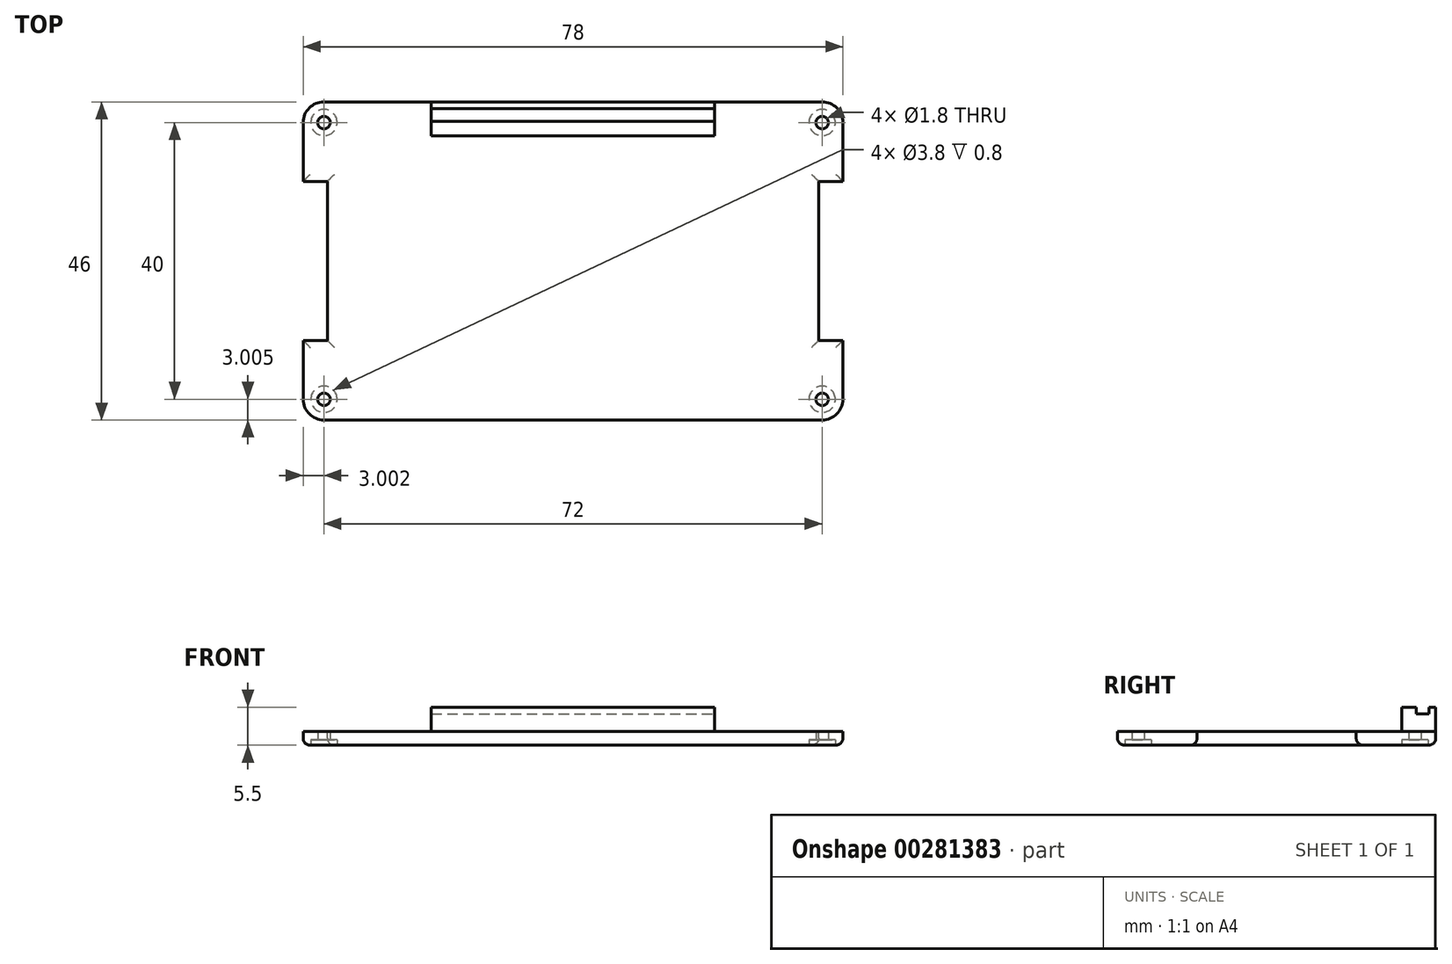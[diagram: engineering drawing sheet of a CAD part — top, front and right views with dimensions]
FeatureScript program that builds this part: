
annotation { "Feature Type Name" : "Feature", "Feature Type Description" : "" }
export const myFeature = defineFeature(function(context is Context, id is Id, definition is map)
    precondition{}
    {
        {
            var Q0;
            Q0=qCreatedBy(makeId("Top.planeOp"),FACE);
            var sketch = newSketch(context, id + "F0", { "sketchPlane" : qUnion([Q0])});
            skLineSegment(sketch, "E0.bottom", {"start": v(-44.88, 28.76) * mm, "end": v(33.12, 28.76) * mm});
            skLineSegment(sketch, "E0.top", {"start": v(-44.88, -17.24) * mm, "end": v(33.12, -17.24) * mm});
            skLineSegment(sketch, "E0.left", {"start": v(-44.88, 28.76) * mm, "end": v(-44.88, -17.24) * mm});
            skLineSegment(sketch, "E0.right", {"start": v(33.12, 28.76) * mm, "end": v(33.12, -17.24) * mm});
            skLineSegment(sketch, "E1.bottom", {"start": v(-44.88, 17.26) * mm, "end": v(-41.38, 17.26) * mm});
            skLineSegment(sketch, "E1.top", {"start": v(-44.88, -5.74) * mm, "end": v(-41.38, -5.74) * mm});
            skLineSegment(sketch, "E1.left", {"start": v(-44.88, 17.26) * mm, "end": v(-44.88, -5.74) * mm});
            skLineSegment(sketch, "E1.right", {"start": v(-41.38, 17.26) * mm, "end": v(-41.38, -5.74) * mm});
            skLineSegment(sketch, "E2.bottom", {"start": v(33.12, 17.26) * mm, "end": v(29.62, 17.26) * mm});
            skLineSegment(sketch, "E2.top", {"start": v(33.12, -5.74) * mm, "end": v(29.62, -5.74) * mm});
            skLineSegment(sketch, "E2.left", {"start": v(33.12, 17.26) * mm, "end": v(33.12, -5.74) * mm});
            skLineSegment(sketch, "E2.right", {"start": v(29.62, 17.26) * mm, "end": v(29.62, -5.74) * mm});
            skSolve(sketch);
        }
        {
            var Q0;
            {var subQ7=sQuery(id+"F0.wireOp",EDGE,"E0.bottom");Q0=makeQuery(id+"F0.imprint","IMPRINT",FACE,{"disambiguationData":[TD([[makeQuery(id+"F0.imprint","IMPRINT",EDGE,{"derivedFrom":subQ7}),-1.0]])]});}
            extrude(context, id + "F1", {"entities" : qUnion([Q0]), "depth" : 2 * mm});
        }
        {
            var Q0;
            Q0=makeQuery(id+"F1.opExtrude","SWEPT_EDGE",EDGE,{"disambiguationData":[OSD([sQuery(id+"F0.wireOp",EDGE,"E0.bottom"),sQuery(id+"F0.wireOp",EDGE,"E0.left")])]});
            var Q1;
            Q1=makeQuery(id+"F1.opExtrude","SWEPT_EDGE",EDGE,{"disambiguationData":[OSD([sQuery(id+"F0.wireOp",EDGE,"E0.bottom"),sQuery(id+"F0.wireOp",EDGE,"E0.right")])]});
            var Q2;
            Q2=makeQuery(id+"F1.opExtrude","SWEPT_EDGE",EDGE,{"disambiguationData":[OSD([sQuery(id+"F0.wireOp",EDGE,"E0.top"),sQuery(id+"F0.wireOp",EDGE,"E0.right")])]});
            var Q3;
            Q3=makeQuery(id+"F1.opExtrude","SWEPT_EDGE",EDGE,{"disambiguationData":[OSD([sQuery(id+"F0.wireOp",EDGE,"E0.top"),sQuery(id+"F0.wireOp",EDGE,"E0.left")])]});
            fillet(context, id + "F2", {"entities" : qUnion([Q0, Q1, Q2, Q3]), "radius" : 3 * mm, "tangentPropagation" : true, "allowEdgeOverflow" : false});
        }
        {
            var Q0;
            Q0=makeQuery(id+"F1.opExtrude","CAP_FACE",FACE,{"disambiguationData":[OSD([sQuery(id+"F0.wireOp",EDGE,"E0.bottom"),sQuery(id+"F0.wireOp",EDGE,"E0.top"),sQuery(id+"F0.wireOp",EDGE,"E0.left"),sQuery(id+"F0.wireOp",EDGE,"E0.right"),sQuery(id+"F0.wireOp",EDGE,"E1.bottom"),sQuery(id+"F0.wireOp",EDGE,"E1.top"),sQuery(id+"F0.wireOp",EDGE,"E1.right"),sQuery(id+"F0.wireOp",EDGE,"E2.bottom"),sQuery(id+"F0.wireOp",EDGE,"E2.top"),sQuery(id+"F0.wireOp",EDGE,"E2.right")])],"isStart":false});
            var sketch = newSketch(context, id + "F3", { "sketchPlane" : qUnion([Q0])});
            skCircle(sketch, "E3", {"center": v(-41.88, 25.76) * mm, "radius": 0.9 * mm});
            skCircle(sketch, "E4", {"center": v(-41.88, -14.24) * mm, "radius": 0.9 * mm});
            skCircle(sketch, "E5", {"center": v(30.12, -14.24) * mm, "radius": 0.9 * mm});
            skCircle(sketch, "E6", {"center": v(30.12, 25.76) * mm, "radius": 0.9 * mm});
            skCircle(sketch, "E7", {"center": v(30.12, -14.24) * mm, "radius": 1.9 * mm});
            skCircle(sketch, "E8", {"center": v(-41.88, -14.24) * mm, "radius": 1.9 * mm});
            skCircle(sketch, "E9", {"center": v(-41.88, 25.76) * mm, "radius": 1.9 * mm});
            skCircle(sketch, "E10", {"center": v(30.12, 25.76) * mm, "radius": 1.9 * mm});
            skSolve(sketch);
        }
        {
            var Q0;
            Q0=makeQuery(id+"F3.imprint","IMPRINT",FACE,{"disambiguationData":[TD([[makeQuery(id+"F3.imprint","IMPRINT",EDGE,{"derivedFrom":sQuery(id+"F3.wireOp",EDGE,"E4")}),1.0]])]});
            var Q1;
            Q1=makeQuery(id+"F3.imprint","IMPRINT",FACE,{"disambiguationData":[TD([[makeQuery(id+"F3.imprint","IMPRINT",EDGE,{"derivedFrom":sQuery(id+"F3.wireOp",EDGE,"E5")}),1.0]])]});
            var Q2;
            Q2=makeQuery(id+"F3.imprint","IMPRINT",FACE,{"disambiguationData":[TD([[makeQuery(id+"F3.imprint","IMPRINT",EDGE,{"derivedFrom":sQuery(id+"F3.wireOp",EDGE,"E6")}),1.0]])]});
            var Q3;
            Q3=makeQuery(id+"F3.imprint","IMPRINT",FACE,{"disambiguationData":[TD([[makeQuery(id+"F3.imprint","IMPRINT",EDGE,{"derivedFrom":sQuery(id+"F3.wireOp",EDGE,"E3")}),1.0]])]});
            extrude(context, id + "F4", {"entities" : qUnion([Q0, Q1, Q2, Q3]), "operationType" : NewBodyOperationType.REMOVE, "oppositeDirection" : true, "depth" : 2.5 * mm});
        }
        {
            var Q0;
            {var subQ0=sQuery(id+"F0.wireOp",EDGE,"E0.right");Q0=makeQuery(id+"F1.opExtrude","CAP_EDGE",EDGE,{"disambiguationData":[OSD([subQ0]),TDD([makeQuery(id+"F0.imprint","IMPRINT",EDGE,{"disambiguationData":[TD([[makeQuery(id+"F0.imprint","INTERSECT",VERTEX,{"derivedFrom":[sQuery(id+"F0.wireOp",EDGE,"E0.top"),subQ0]}),1.0]])],"derivedFrom":subQ0})])],"isStart":false});}
            var Q1;
            {var subQ0=sQuery(id+"F0.wireOp",EDGE,"E0.right");var subQ1=sQuery(id+"F0.wireOp",EDGE,"E0.top");Q1=makeQuery(id+"F2.opFillet","BLEND_EDGE",EDGE,{"blendedFrom":[makeQuery(id+"F1.opExtrude","SWEPT_EDGE",EDGE,{"disambiguationData":[OSD([subQ1,subQ0])]}),makeQuery(id+"F1.opExtrude","CAP_FACE",FACE,{"disambiguationData":[OSD([sQuery(id+"F0.wireOp",EDGE,"E0.bottom"),subQ1,sQuery(id+"F0.wireOp",EDGE,"E0.left"),subQ0,sQuery(id+"F0.wireOp",EDGE,"E1.bottom"),sQuery(id+"F0.wireOp",EDGE,"E1.top"),sQuery(id+"F0.wireOp",EDGE,"E1.right"),sQuery(id+"F0.wireOp",EDGE,"E2.bottom"),sQuery(id+"F0.wireOp",EDGE,"E2.top"),sQuery(id+"F0.wireOp",EDGE,"E2.right")])],"isStart":false})],"blendedInto":[makeQuery(id+"F1.opExtrude","CAP_FACE",FACE,{"disambiguationData":[OSD([sQuery(id+"F0.wireOp",EDGE,"E0.bottom"),subQ1,sQuery(id+"F0.wireOp",EDGE,"E0.left"),subQ0,sQuery(id+"F0.wireOp",EDGE,"E1.bottom"),sQuery(id+"F0.wireOp",EDGE,"E1.top"),sQuery(id+"F0.wireOp",EDGE,"E1.right"),sQuery(id+"F0.wireOp",EDGE,"E2.bottom"),sQuery(id+"F0.wireOp",EDGE,"E2.top"),sQuery(id+"F0.wireOp",EDGE,"E2.right")])],"isStart":false})]});}
            var Q2;
            Q2=makeQuery(id+"F1.opExtrude","CAP_EDGE",EDGE,{"disambiguationData":[OSD([sQuery(id+"F0.wireOp",EDGE,"E2.top")])],"isStart":false});
            var Q3;
            Q3=makeQuery(id+"F1.opExtrude","CAP_EDGE",EDGE,{"disambiguationData":[OSD([sQuery(id+"F0.wireOp",EDGE,"E2.right")])],"isStart":false});
            var Q4;
            Q4=makeQuery(id+"F1.opExtrude","CAP_EDGE",EDGE,{"disambiguationData":[OSD([sQuery(id+"F0.wireOp",EDGE,"E2.bottom")])],"isStart":false});
            var Q5;
            {var subQ0=sQuery(id+"F0.wireOp",EDGE,"E0.right");Q5=makeQuery(id+"F1.opExtrude","CAP_EDGE",EDGE,{"disambiguationData":[OSD([subQ0]),TDD([makeQuery(id+"F0.imprint","IMPRINT",EDGE,{"disambiguationData":[TD([[makeQuery(id+"F0.imprint","INTERSECT",VERTEX,{"derivedFrom":[sQuery(id+"F0.wireOp",EDGE,"E0.bottom"),subQ0]}),-1.0]])],"derivedFrom":subQ0})])],"isStart":false});}
            var Q6;
            Q6=makeQuery(id+"F1.opExtrude","CAP_EDGE",EDGE,{"disambiguationData":[OSD([sQuery(id+"F0.wireOp",EDGE,"E1.bottom")])],"isStart":false});
            var Q7;
            Q7=makeQuery(id+"F1.opExtrude","CAP_EDGE",EDGE,{"disambiguationData":[OSD([sQuery(id+"F0.wireOp",EDGE,"E1.right")])],"isStart":false});
            var Q8;
            Q8=makeQuery(id+"F1.opExtrude","CAP_EDGE",EDGE,{"disambiguationData":[OSD([sQuery(id+"F0.wireOp",EDGE,"E1.top")])],"isStart":false});
            fillet(context, id + "F5", {"entities" : qUnion([Q0, Q1, Q2, Q3, Q4, Q5, Q6, Q7, Q8]), "radius" : 1 * mm, "tangentPropagation" : true, "allowEdgeOverflow" : false});
        }
        {
            var Q0;
            Q0=makeQuery(id+"F1.opExtrude","CAP_FACE",FACE,{"disambiguationData":[OSD([sQuery(id+"F0.wireOp",EDGE,"E0.bottom"),sQuery(id+"F0.wireOp",EDGE,"E0.top"),sQuery(id+"F0.wireOp",EDGE,"E0.left"),sQuery(id+"F0.wireOp",EDGE,"E0.right"),sQuery(id+"F0.wireOp",EDGE,"E1.bottom"),sQuery(id+"F0.wireOp",EDGE,"E1.top"),sQuery(id+"F0.wireOp",EDGE,"E1.right"),sQuery(id+"F0.wireOp",EDGE,"E2.bottom"),sQuery(id+"F0.wireOp",EDGE,"E2.top"),sQuery(id+"F0.wireOp",EDGE,"E2.right")])],"isStart":true});
            var sketch = newSketch(context, id + "F6", { "sketchPlane" : qUnion([Q0])});
            skLineSegment(sketch, "E11.bottom", {"start": v(-26.36, 17.24) * mm, "end": v(14.6, 17.24) * mm});
            skLineSegment(sketch, "E11.top", {"start": v(-26.36, 12.34) * mm, "end": v(14.6, 12.34) * mm});
            skLineSegment(sketch, "E11.left", {"start": v(-26.36, 17.24) * mm, "end": v(-26.36, 12.34) * mm});
            skLineSegment(sketch, "E11.right", {"start": v(14.6, 17.24) * mm, "end": v(14.6, 12.34) * mm});
            skSolve(sketch);
        }
        {
            var Q0;
            Q0=makeQuery(id+"F6.imprint","IMPRINT",FACE,{"disambiguationData":[TD([[makeQuery(id+"F6.imprint","IMPRINT",EDGE,{"derivedFrom":sQuery(id+"F6.wireOp",EDGE,"E11.bottom")}),-1.0]])]});
            extrude(context, id + "F7", {"entities" : qUnion([Q0]), "operationType" : NewBodyOperationType.ADD, "depth" : 3.5 * mm});
        }
        {
            var Q0;
            Q0=makeQuery(id+"F7.opExtrude","CAP_FACE",FACE,{"disambiguationData":[OSD([sQuery(id+"F6.wireOp",EDGE,"E11.bottom"),sQuery(id+"F6.wireOp",EDGE,"E11.top"),sQuery(id+"F6.wireOp",EDGE,"E11.left"),sQuery(id+"F6.wireOp",EDGE,"E11.right")])],"isStart":false});
            var sketch = newSketch(context, id + "F8", { "sketchPlane" : qUnion([Q0])});
            skLineSegment(sketch, "E12.bottom", {"start": v(-26.36, 16.24) * mm, "end": v(14.6, 16.24) * mm});
            skLineSegment(sketch, "E12.top", {"start": v(-26.36, 14.44) * mm, "end": v(14.6, 14.44) * mm});
            skLineSegment(sketch, "E12.left", {"start": v(-26.36, 16.24) * mm, "end": v(-26.36, 14.44) * mm});
            skLineSegment(sketch, "E12.right", {"start": v(14.6, 16.24) * mm, "end": v(14.6, 14.44) * mm});
            skSolve(sketch);
        }
        {
            var Q0;
            Q0=makeQuery(id+"F8.imprint","IMPRINT",FACE,{"disambiguationData":[TD([[makeQuery(id+"F8.imprint","IMPRINT",EDGE,{"derivedFrom":sQuery(id+"F8.wireOp",EDGE,"E12.bottom")}),-1.0]])]});
            extrude(context, id + "F9", {"entities" : qUnion([Q0]), "operationType" : NewBodyOperationType.REMOVE, "oppositeDirection" : true, "depth" : 1 * mm});
        }
        {
            var Q0;
            Q0=makeQuery(id+"F1.opExtrude","SWEPT_BODY",BODY,{"disambiguationData":[OSD([sQuery(id+"F0.wireOp",EDGE,"E0.bottom"),sQuery(id+"F0.wireOp",EDGE,"E0.top"),sQuery(id+"F0.wireOp",EDGE,"E0.left"),sQuery(id+"F0.wireOp",EDGE,"E0.right"),sQuery(id+"F0.wireOp",EDGE,"E1.bottom"),sQuery(id+"F0.wireOp",EDGE,"E1.top"),sQuery(id+"F0.wireOp",EDGE,"E1.right"),sQuery(id+"F0.wireOp",EDGE,"E2.bottom"),sQuery(id+"F0.wireOp",EDGE,"E2.top"),sQuery(id+"F0.wireOp",EDGE,"E2.right")])]});
            var Q1;
            Q1=makeQuery(id+"F1.opExtrude","CAP_EDGE",EDGE,{"disambiguationData":[OSD([sQuery(id+"F0.wireOp",EDGE,"E0.bottom")])],"isStart":true});
            transform(context, id + "F10", {"entities" : qUnion([Q0]), "transformType" : TransformType.ROTATION, "transformAxis" : qUnion([Q1]), "angle" : 180 * degree, "makeCopy" : false});
        }
        {
            var Q0;
            Q0=makeQuery(id+"F1.opExtrude","SWEPT_BODY",BODY,{"disambiguationData":[OSD([sQuery(id+"F0.wireOp",EDGE,"E0.bottom"),sQuery(id+"F0.wireOp",EDGE,"E0.top"),sQuery(id+"F0.wireOp",EDGE,"E0.left"),sQuery(id+"F0.wireOp",EDGE,"E0.right"),sQuery(id+"F0.wireOp",EDGE,"E1.bottom"),sQuery(id+"F0.wireOp",EDGE,"E1.top"),sQuery(id+"F0.wireOp",EDGE,"E1.right"),sQuery(id+"F0.wireOp",EDGE,"E2.bottom"),sQuery(id+"F0.wireOp",EDGE,"E2.top"),sQuery(id+"F0.wireOp",EDGE,"E2.right")])]});
            transform(context, id + "F11", {"entities" : qUnion([Q0]), "transformType" : TransformType.TRANSLATION_3D, "dx" : 0 * mm, "dy" : 0 * mm, "dz" : 2 * mm, "makeCopy" : false});
        }
        {
            var Q0;
            Q0=makeQuery(id+"F1.opExtrude","CAP_FACE",FACE,{"disambiguationData":[OSD([sQuery(id+"F0.wireOp",EDGE,"E0.bottom"),sQuery(id+"F0.wireOp",EDGE,"E0.top"),sQuery(id+"F0.wireOp",EDGE,"E0.left"),sQuery(id+"F0.wireOp",EDGE,"E0.right"),sQuery(id+"F0.wireOp",EDGE,"E1.bottom"),sQuery(id+"F0.wireOp",EDGE,"E1.top"),sQuery(id+"F0.wireOp",EDGE,"E1.right"),sQuery(id+"F0.wireOp",EDGE,"E2.bottom"),sQuery(id+"F0.wireOp",EDGE,"E2.top"),sQuery(id+"F0.wireOp",EDGE,"E2.right")])],"isStart":false});
            var sketch = newSketch(context, id + "F12", { "sketchPlane" : qUnion([Q0])});
            skCircle(sketch, "E13", {"center": v(-41.88, -31.76) * mm, "radius": 1.9 * mm});
            skCircle(sketch, "E14", {"center": v(-41.88, -71.76) * mm, "radius": 1.9 * mm});
            skCircle(sketch, "E15", {"center": v(30.12, -71.76) * mm, "radius": 1.9 * mm});
            skCircle(sketch, "E16", {"center": v(30.12, -31.76) * mm, "radius": 1.9 * mm});
            skSolve(sketch);
        }
        {
            var Q0;
            Q0 = qSketchRegion(id + "F12", true);
            extrude(context, id + "F13", {"entities" : qUnion([Q0]), "operationType" : NewBodyOperationType.REMOVE, "oppositeDirection" : true, "depth" : .8 * mm});
        }
    });
